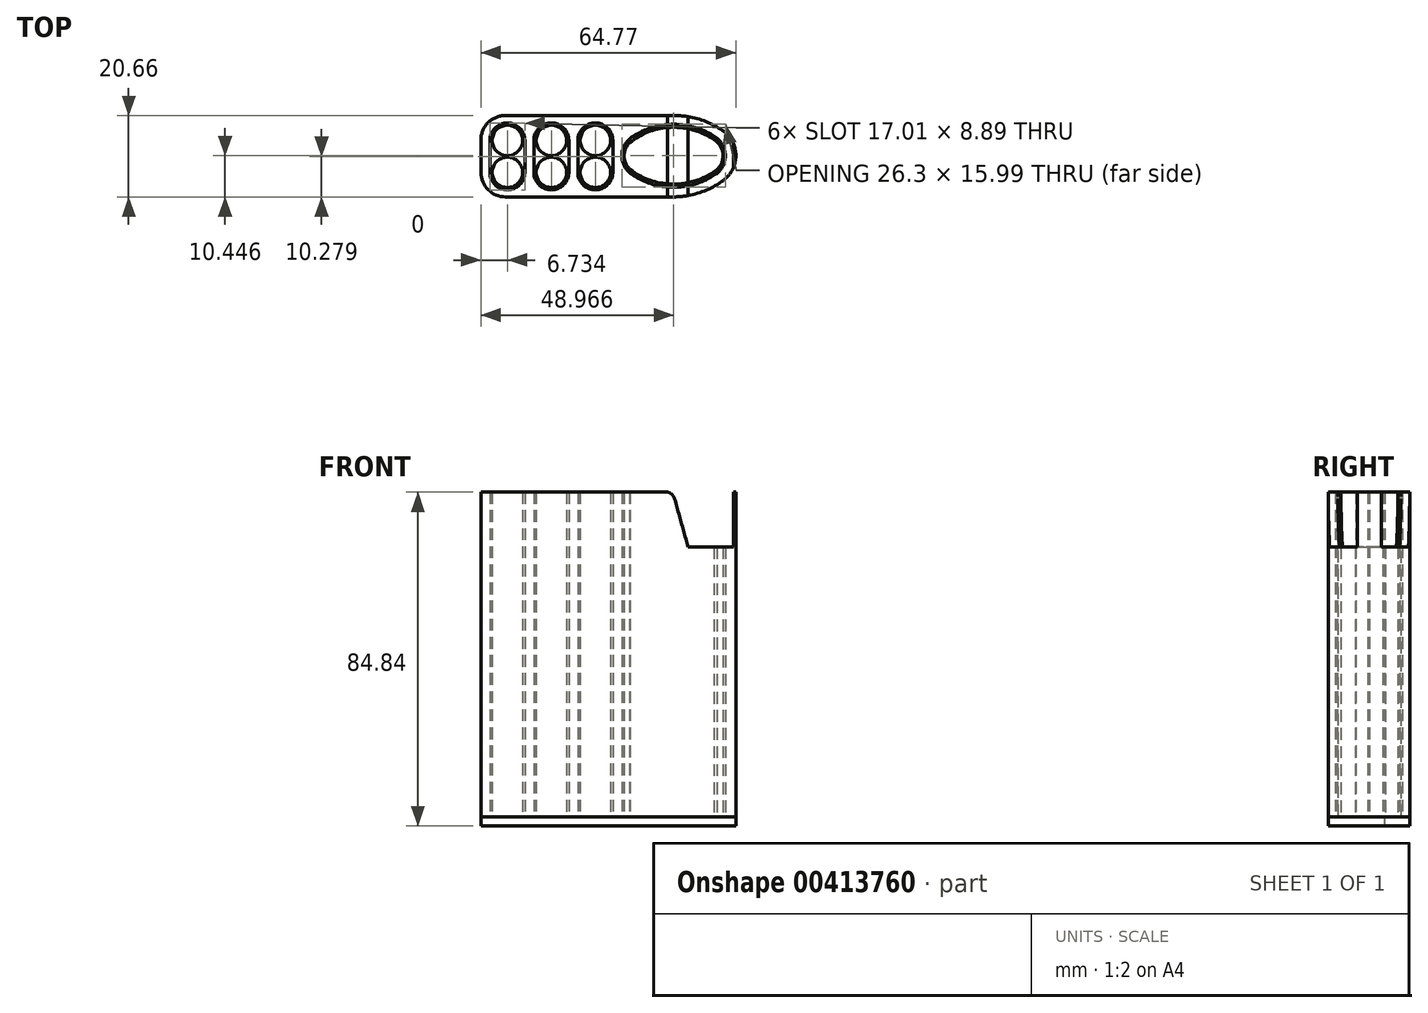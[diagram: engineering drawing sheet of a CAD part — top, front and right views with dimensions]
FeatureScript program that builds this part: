
annotation { "Feature Type Name" : "Feature", "Feature Type Description" : "" }
export const myFeature = defineFeature(function(context is Context, id is Id, definition is map)
    precondition{}
    {
        {
            var Q0;
            Q0=qCreatedBy(makeId("Top.planeOp"),FACE);
            var sketch = newSketch(context, id + "F0", { "sketchPlane" : qUnion([Q0])});
            skArc(sketch, "E0.0", {"start": v(-7.17, -3.47) * mm, "mid": v(3.83, -7.2) * mm, "end": v(14.84, -3.5) * mm});
            skArc(sketch, "E0.1", {"start": v(-7.3, 3.42) * mm, "mid": v(-8.73, -0.05) * mm, "end": v(-7.17, -3.47) * mm});
            skArc(sketch, "E0.2", {"start": v(14.1, 4.11) * mm, "mid": v(3.28, 7.26) * mm, "end": v(-7.3, 3.42) * mm});
            skArc(sketch, "E0.3", {"start": v(14.84, -3.5) * mm, "mid": v(16.4, 0.5) * mm, "end": v(14.1, 4.11) * mm});
            skArc(sketch, "E1", {"start": v(-20.48, -4.2) * mm, "mid": v(-16.03, -8.64) * mm, "end": v(-11.59, -4.2) * mm});
            skArc(sketch, "E2", {"start": v(-11.59, 3.93) * mm, "mid": v(-16.03, 8.37) * mm, "end": v(-20.48, 3.93) * mm});
            skLineSegment(sketch, "E3", {"start": v(-11.59, 3.93) * mm, "end": v(-11.59, -4.2) * mm});
            skLineSegment(sketch, "E4", {"start": v(-20.48, 3.93) * mm, "end": v(-20.48, -4.2) * mm});
            skArc(sketch, "E5.0", {"start": v(14.5, 4.76) * mm, "mid": v(3.84, 8.03) * mm, "end": v(-6.81, 4.73) * mm});
            skArc(sketch, "E6.0", {"start": v(-6.84, -4.65) * mm, "mid": v(3.85, -7.96) * mm, "end": v(14.53, -4.65) * mm});
            skLineSegment(sketch, "E7", {"start": v(-16.03, 3.93) * mm, "end": v(-16.03, -4.2) * mm});
            skLineSegment(sketch, "E8", {"start": v(-16.03, 3.93) * mm, "end": v(-16.03, -0.13) * mm});
            skPoint(sketch, "E9.startSnap0", {"position": v(3.85, -7.96) * mm});
            skLineSegment(sketch, "E10", {"start": v(-9.3, -0.14) * mm, "end": v(-11.59, -0.14) * mm});
            skArc(sketch, "E11", {"start": v(-31.66, -4.2) * mm, "mid": v(-27.21, -8.64) * mm, "end": v(-22.77, -4.2) * mm});
            skArc(sketch, "E12", {"start": v(-22.77, 3.93) * mm, "mid": v(-27.21, 8.37) * mm, "end": v(-31.66, 3.93) * mm});
            skLineSegment(sketch, "E13", {"start": v(-22.77, 3.93) * mm, "end": v(-22.77, -4.2) * mm});
            skLineSegment(sketch, "E14", {"start": v(-31.66, 3.93) * mm, "end": v(-31.66, -4.2) * mm});
            skLineSegment(sketch, "E15", {"start": v(-27.21, 3.93) * mm, "end": v(-27.21, -4.2) * mm});
            skLineSegment(sketch, "E16", {"start": v(-27.21, 3.93) * mm, "end": v(-27.21, -0.13) * mm});
            skLineSegment(sketch, "E17", {"start": v(-31.66, -0.13) * mm, "end": v(-33.94, -0.13) * mm});
            skArc(sketch, "E18", {"start": v(-42.83, -4.2) * mm, "mid": v(-38.39, -8.64) * mm, "end": v(-33.94, -4.2) * mm});
            skArc(sketch, "E19", {"start": v(-33.94, 3.93) * mm, "mid": v(-38.39, 8.37) * mm, "end": v(-42.83, 3.93) * mm});
            skLineSegment(sketch, "E20", {"start": v(-33.94, 3.93) * mm, "end": v(-33.94, -4.2) * mm});
            skLineSegment(sketch, "E21", {"start": v(-42.83, 3.93) * mm, "end": v(-42.83, -4.2) * mm});
            skLineSegment(sketch, "E22", {"start": v(-38.39, 3.93) * mm, "end": v(-38.39, -4.2) * mm});
            skLineSegment(sketch, "E23", {"start": v(-38.39, 3.93) * mm, "end": v(-38.39, -0.13) * mm});
            skLineSegment(sketch, "E24", {"start": v(-22.77, -0.13) * mm, "end": v(-20.48, -0.13) * mm});
            skLineSegment(sketch, "E25", {"start": v(-4, 0.04) * mm, "end": v(11.68, 0.04) * mm});
            skLineSegment(sketch, "E26.0", {"start": v(-45.12, 3.93) * mm, "end": v(-45.12, -4.2) * mm});
            skLineSegment(sketch, "E27.0", {"start": v(-38.9, 10.25) * mm, "end": v(4.07, 10.25) * mm});
            skLineSegment(sketch, "E28.0", {"start": v(3.73, -10.41) * mm, "end": v(-38.9, -10.41) * mm});
            skArc(sketch, "E29.0", {"start": v(16.48, -6.23) * mm, "mid": v(19.65, 0.16) * mm, "end": v(16.28, 6.45) * mm});
            skArc(sketch, "E30", {"start": v(-38.9, 10.25) * mm, "mid": v(-43.33, 8.4) * mm, "end": v(-45.12, 3.93) * mm});
            skArc(sketch, "E31", {"start": v(-45.12, -4.2) * mm, "mid": v(-43.3, -8.6) * mm, "end": v(-38.9, -10.41) * mm});
            skArc(sketch, "E32", {"start": v(3.73, -10.41) * mm, "mid": v(10.44, -9.34) * mm, "end": v(16.48, -6.23) * mm});
            skArc(sketch, "E33", {"start": v(16.28, 6.45) * mm, "mid": v(10.46, 9.28) * mm, "end": v(4.07, 10.25) * mm});
            skCircle(sketch, "E34", {"center": v(-16.03, 3.93) * mm, "radius": 3.87 * mm});
            skCircle(sketch, "E35", {"center": v(-16.03, -4.2) * mm, "radius": 3.87 * mm});
            skCircle(sketch, "E36", {"center": v(-27.21, -4.2) * mm, "radius": 3.87 * mm});
            skCircle(sketch, "E37", {"center": v(-27.21, 3.93) * mm, "radius": 3.87 * mm});
            skCircle(sketch, "E38", {"center": v(-38.39, -4.2) * mm, "radius": 3.87 * mm});
            skCircle(sketch, "E39", {"center": v(-38.39, 3.93) * mm, "radius": 3.87 * mm});
            skArc(sketch, "E40", {"start": v(-6.81, 4.73) * mm, "mid": v(-9.3, 0.04) * mm, "end": v(-6.84, -4.65) * mm});
            skArc(sketch, "E41", {"start": v(14.53, -4.65) * mm, "mid": v(17, 0.06) * mm, "end": v(14.5, 4.76) * mm});
            skSolve(sketch);
        }
        {
            var Q0;
            Q0=makeQuery(id+"F0.imprint","IMPRINT",FACE,{"disambiguationData":[TD([[makeQuery(id+"F0.imprint","IMPRINT",EDGE,{"derivedFrom":sQuery(id+"F0.wireOp",EDGE,"E0.0")}),-1.0]])]});
            var Q1;
            Q1=makeQuery(id+"F0.imprint","IMPRINT",FACE,{"disambiguationData":[TD([[makeQuery(id+"F0.imprint","IMPRINT",EDGE,{"derivedFrom":sQuery(id+"F0.wireOp",EDGE,"E39")}),1.0]])]});
            var Q2;
            Q2=makeQuery(id+"F0.imprint","IMPRINT",FACE,{"disambiguationData":[TD([[makeQuery(id+"F0.imprint","IMPRINT",EDGE,{"derivedFrom":sQuery(id+"F0.wireOp",EDGE,"E38")}),1.0]])]});
            var Q3;
            {var subQ2=sQuery(id+"F0.wireOp",EDGE,"E18");Q3=makeQuery(id+"F0.imprint","IMPRINT",FACE,{"disambiguationData":[TD([[makeQuery(id+"F0.imprint","IMPRINT",EDGE,{"derivedFrom":subQ2}),1.0]])]});}
            var Q4;
            {var subQ1=sQuery(id+"F0.wireOp",EDGE,"E11");Q4=makeQuery(id+"F0.imprint","IMPRINT",FACE,{"disambiguationData":[TD([[makeQuery(id+"F0.imprint","IMPRINT",EDGE,{"derivedFrom":subQ1}),1.0]])]});}
            var Q5;
            Q5=makeQuery(id+"F0.imprint","IMPRINT",FACE,{"disambiguationData":[TD([[makeQuery(id+"F0.imprint","IMPRINT",EDGE,{"derivedFrom":sQuery(id+"F0.wireOp",EDGE,"E37")}),1.0]])]});
            var Q6;
            Q6=makeQuery(id+"F0.imprint","IMPRINT",FACE,{"disambiguationData":[TD([[makeQuery(id+"F0.imprint","IMPRINT",EDGE,{"derivedFrom":sQuery(id+"F0.wireOp",EDGE,"E36")}),1.0]])]});
            var Q7;
            {var subQ1=sQuery(id+"F0.wireOp",EDGE,"E1");Q7=makeQuery(id+"F0.imprint","IMPRINT",FACE,{"disambiguationData":[TD([[makeQuery(id+"F0.imprint","IMPRINT",EDGE,{"derivedFrom":subQ1}),1.0]])]});}
            var Q8;
            Q8=makeQuery(id+"F0.imprint","IMPRINT",FACE,{"disambiguationData":[TD([[makeQuery(id+"F0.imprint","IMPRINT",EDGE,{"derivedFrom":sQuery(id+"F0.wireOp",EDGE,"E34")}),1.0]])]});
            var Q9;
            Q9=makeQuery(id+"F0.imprint","IMPRINT",FACE,{"disambiguationData":[TD([[makeQuery(id+"F0.imprint","IMPRINT",EDGE,{"derivedFrom":sQuery(id+"F0.wireOp",EDGE,"E35")}),1.0]])]});
            var Q10;
            Q10=makeQuery(id+"F0.imprint","IMPRINT",FACE,{"disambiguationData":[TD([[makeQuery(id+"F0.imprint","IMPRINT",EDGE,{"derivedFrom":sQuery(id+"F0.wireOp",EDGE,"E0.0")}),1.0]])]});
            var Q11;
            {var subQ11=sQuery(id+"F0.wireOp",EDGE,"E1");Q11=makeQuery(id+"F0.imprint","IMPRINT",FACE,{"disambiguationData":[TD([[makeQuery(id+"F0.imprint","IMPRINT",EDGE,{"derivedFrom":subQ11}),-1.0]])]});}
            extrude(context, id + "F1", {"entities" : qUnion([Q0, Q1, Q2, Q3, Q4, Q5, Q6, Q7, Q8, Q9, Q10, Q11]), "oppositeDirection" : true, "depth" : 2.3 * mm});
        }
        {
            var Q0;
            Q0=makeQuery(id+"F0.imprint","IMPRINT",FACE,{"disambiguationData":[TD([[makeQuery(id+"F0.imprint","IMPRINT",EDGE,{"derivedFrom":sQuery(id+"F0.wireOp",EDGE,"E39")}),1.0]])]});
            var Q1;
            Q1=makeQuery(id+"F0.imprint","IMPRINT",FACE,{"disambiguationData":[TD([[makeQuery(id+"F0.imprint","IMPRINT",EDGE,{"derivedFrom":sQuery(id+"F0.wireOp",EDGE,"E38")}),1.0]])]});
            var Q2;
            Q2=makeQuery(id+"F0.imprint","IMPRINT",FACE,{"disambiguationData":[TD([[makeQuery(id+"F0.imprint","IMPRINT",EDGE,{"derivedFrom":sQuery(id+"F0.wireOp",EDGE,"E37")}),1.0]])]});
            var Q3;
            Q3=makeQuery(id+"F0.imprint","IMPRINT",FACE,{"disambiguationData":[TD([[makeQuery(id+"F0.imprint","IMPRINT",EDGE,{"derivedFrom":sQuery(id+"F0.wireOp",EDGE,"E36")}),1.0]])]});
            var Q4;
            Q4=makeQuery(id+"F0.imprint","IMPRINT",FACE,{"disambiguationData":[TD([[makeQuery(id+"F0.imprint","IMPRINT",EDGE,{"derivedFrom":sQuery(id+"F0.wireOp",EDGE,"E34")}),1.0]])]});
            var Q5;
            Q5=makeQuery(id+"F0.imprint","IMPRINT",FACE,{"disambiguationData":[TD([[makeQuery(id+"F0.imprint","IMPRINT",EDGE,{"derivedFrom":sQuery(id+"F0.wireOp",EDGE,"E35")}),1.0]])]});
            extrude(context, id + "F2", {"entities" : qUnion([Q0, Q1, Q2, Q3, Q4, Q5]), "depth" : 82.55 * mm});
        }
        {
            var Q0;
            Q0=makeQuery(id+"F0.imprint","IMPRINT",FACE,{"disambiguationData":[TD([[makeQuery(id+"F0.imprint","IMPRINT",EDGE,{"derivedFrom":sQuery(id+"F0.wireOp",EDGE,"E0.0")}),1.0]])]});
            extrude(context, id + "F3", {"entities" : qUnion([Q0]), "depth" : 82.55 * mm});
        }
        {
            var Q0;
            {var subQ11=sQuery(id+"F0.wireOp",EDGE,"E1");Q0=makeQuery(id+"F0.imprint","IMPRINT",FACE,{"disambiguationData":[TD([[makeQuery(id+"F0.imprint","IMPRINT",EDGE,{"derivedFrom":subQ11}),-1.0]])]});}
            extrude(context, id + "F4", {"entities" : qUnion([Q0]), "depth" : 82.55 * mm});
        }
        {
            var Q0;
            Q0=qCreatedBy(makeId("Front.planeOp"),FACE);
            var sketch = newSketch(context, id + "F5", { "sketchPlane" : qUnion([Q0])});
            skLineSegment(sketch, "E42", {"start": v(16.41, 0) * mm, "end": v(16.41, 68.58) * mm});
            skLineSegment(sketch, "E43", {"start": v(16.41, 68.58) * mm, "end": v(7.52, 68.58) * mm});
            skLineSegment(sketch, "E44", {"start": v(7.52, 68.58) * mm, "end": v(4.12, 80.77) * mm});
            skLineSegment(sketch, "E45", {"start": v(1.68, 82.62) * mm, "end": v(-10.36, 82.62) * mm});
            skPoint(sketch, "E46.visualSharp", {"position": v(3.6, 82.62) * mm});
            skArc(sketch, "E46.filletArc", {"start": v(4.12, 80.77) * mm, "mid": v(3.21, 82.1) * mm, "end": v(1.68, 82.62) * mm});
            skLineSegment(sketch, "E47", {"start": v(-10.36, 82.62) * mm, "end": v(-10.36, 88.6) * mm});
            skLineSegment(sketch, "E48", {"start": v(-10.36, 88.6) * mm, "end": v(16.41, 88.6) * mm});
            skLineSegment(sketch, "E49", {"start": v(16.41, 88.6) * mm, "end": v(19.04, 88.6) * mm});
            skLineSegment(sketch, "E50", {"start": v(19.04, 88.6) * mm, "end": v(19.04, 68.58) * mm});
            skLineSegment(sketch, "E51", {"start": v(19.04, 68.58) * mm, "end": v(16.41, 68.58) * mm});
            skSolve(sketch);
        }
        {
            var Q0;
            Q0=makeQuery(id+"F5.imprint","IMPRINT",FACE,{"disambiguationData":[TD([[makeQuery(id+"F5.imprint","IMPRINT",EDGE,{"derivedFrom":sQuery(id+"F5.wireOp",EDGE,"E43")}),-1.0]])]});
            extrude(context, id + "F6", {"entities" : qUnion([Q0]), "operationType" : NewBodyOperationType.REMOVE, "endBound" : BoundingType.SYMMETRIC, "oppositeDirection" : true, "depth" : 25.4 * mm});
        }
        {
            var Q0;
            Q0=makeQuery(id+"F4.opExtrude","SWEPT_BODY",BODY,{"disambiguationData":[OSD([sQuery(id+"F0.wireOp",EDGE,"E1"),sQuery(id+"F0.wireOp",EDGE,"E2"),sQuery(id+"F0.wireOp",EDGE,"E3"),sQuery(id+"F0.wireOp",EDGE,"E4"),sQuery(id+"F0.wireOp",EDGE,"E5.0"),sQuery(id+"F0.wireOp",EDGE,"E6.0"),sQuery(id+"F0.wireOp",EDGE,"E11"),sQuery(id+"F0.wireOp",EDGE,"E12"),sQuery(id+"F0.wireOp",EDGE,"E13"),sQuery(id+"F0.wireOp",EDGE,"E14"),sQuery(id+"F0.wireOp",EDGE,"E18"),sQuery(id+"F0.wireOp",EDGE,"E19"),sQuery(id+"F0.wireOp",EDGE,"E20"),sQuery(id+"F0.wireOp",EDGE,"E21"),sQuery(id+"F0.wireOp",EDGE,"E26.0"),sQuery(id+"F0.wireOp",EDGE,"E27.0"),sQuery(id+"F0.wireOp",EDGE,"E28.0"),sQuery(id+"F0.wireOp",EDGE,"E29.0"),sQuery(id+"F0.wireOp",EDGE,"E30"),sQuery(id+"F0.wireOp",EDGE,"E31"),sQuery(id+"F0.wireOp",EDGE,"E32"),sQuery(id+"F0.wireOp",EDGE,"E33"),sQuery(id+"F0.wireOp",EDGE,"E40"),sQuery(id+"F0.wireOp",EDGE,"E41")])]});
            transform(context, id + "F7", {"entities" : qUnion([Q0]), "transformType" : TransformType.TRANSLATION_3D, "dx" : 0 * mm, "dy" : 0 * mm, "dz" : 0 * mm, "makeCopy" : true});
        }
    });
